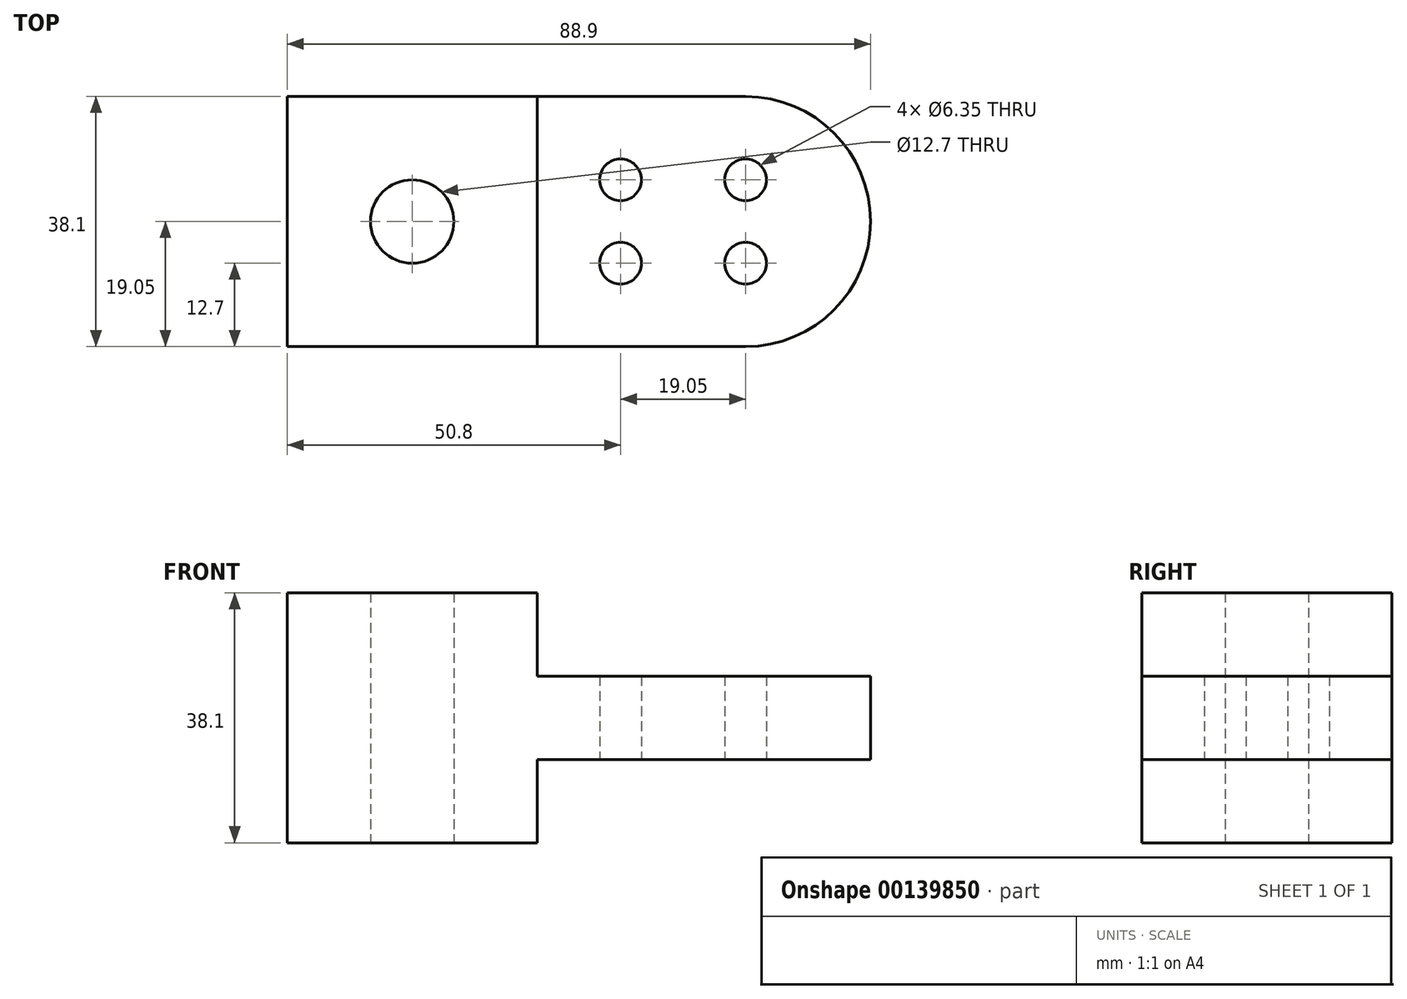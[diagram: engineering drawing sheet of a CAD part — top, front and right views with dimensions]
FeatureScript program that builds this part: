
annotation { "Feature Type Name" : "Feature", "Feature Type Description" : "" }
export const myFeature = defineFeature(function(context is Context, id is Id, definition is map)
    precondition{}
    {
        {
            var Q0;
            Q0=qCreatedBy(makeId("Top.planeOp"),FACE);
            var sketch = newSketch(context, id + "F0", { "sketchPlane" : qUnion([Q0])});
            skLineSegment(sketch, "E0.bottom", {"start": v(-69.85, 0) * mm, "end": v(0, 0) * mm});
            skLineSegment(sketch, "E0.top", {"start": v(-69.85, -38.1) * mm, "end": v(0, -38.1) * mm});
            skLineSegment(sketch, "E0.left", {"start": v(-69.85, 0) * mm, "end": v(-69.85, -38.1) * mm});
            skLineSegment(sketch, "E0.right", {"start": v(0, 0) * mm, "end": v(0, -38.1) * mm});
            skArc(sketch, "E1", {"start": v(0, -38.1) * mm, "mid": v(19.05, -19.05) * mm, "end": v(0, 0) * mm});
            skCircle(sketch, "E2", {"center": v(0, -12.7) * mm, "radius": 3.18 * mm});
            skCircle(sketch, "E3", {"center": v(0, -25.4) * mm, "radius": 3.18 * mm});
            skCircle(sketch, "E4", {"center": v(-19.05, -12.7) * mm, "radius": 3.18 * mm});
            skCircle(sketch, "E5", {"center": v(-19.05, -25.4) * mm, "radius": 3.18 * mm});
            skCircle(sketch, "E6", {"center": v(-50.8, -19.05) * mm, "radius": 6.35 * mm});
            skSolve(sketch);
        }
        {
            var Q0;
            Q0 = qSketchRegion(id + "F0", true);
            extrude(context, id + "F1", {"entities" : qUnion([Q0]), "depth" : 38.1 * mm});
        }
        {
            var Q0;
            Q0=qCreatedBy(makeId("Front.planeOp"),FACE);
            var sketch = newSketch(context, id + "F2", { "sketchPlane" : qUnion([Q0])});
            skLineSegment(sketch, "E7.bottom", {"start": v(0, 0) * mm, "end": v(-31.75, 0) * mm});
            skLineSegment(sketch, "E7.top", {"start": v(0, 12.7) * mm, "end": v(-31.75, 12.7) * mm});
            skLineSegment(sketch, "E7.left", {"start": v(0, 0) * mm, "end": v(0, 12.7) * mm});
            skLineSegment(sketch, "E7.right", {"start": v(-31.75, 0) * mm, "end": v(-31.75, 12.7) * mm});
            skLineSegment(sketch, "E8.bottom", {"start": v(0, 0) * mm, "end": v(19.05, 0) * mm});
            skLineSegment(sketch, "E8.top", {"start": v(0, 12.7) * mm, "end": v(19.05, 12.7) * mm});
            skLineSegment(sketch, "E8.right", {"start": v(19.05, 0) * mm, "end": v(19.05, 12.7) * mm});
            skLineSegment(sketch, "E9.bottom", {"start": v(0, 0) * mm, "end": v(-6.38, 0) * mm});
            skLineSegment(sketch, "E9.top", {"start": v(0, 25.4) * mm, "end": v(-6.38, 25.4) * mm});
            skLineSegment(sketch, "E9.left", {"start": v(0, 0) * mm, "end": v(0, 25.4) * mm});
            skLineSegment(sketch, "E9.right", {"start": v(-6.38, 0) * mm, "end": v(-6.38, 25.4) * mm});
            skLineSegment(sketch, "E10.bottom", {"start": v(0, 25.4) * mm, "end": v(-31.75, 25.4) * mm});
            skLineSegment(sketch, "E10.top", {"start": v(0, 38.1) * mm, "end": v(-31.75, 38.1) * mm});
            skPoint(sketch, "E11.oppositeSnap0", {"position": v(0, 38.1) * mm});
            skLineSegment(sketch, "E11.bottom", {"start": v(0, 25.4) * mm, "end": v(19.05, 25.4) * mm});
            skLineSegment(sketch, "E11.top", {"start": v(0, 38.1) * mm, "end": v(19.05, 38.1) * mm});
            skLineSegment(sketch, "E11.right", {"start": v(19.05, 25.4) * mm, "end": v(19.05, 38.1) * mm});
            skLineSegment(sketch, "E12", {"start": v(-31.75, 38.1) * mm, "end": v(-31.75, 25.4) * mm});
            skSolve(sketch);
        }
        {
            var Q0;
            {var subQ0=sQuery(id+"F2.wireOp",EDGE,"E7.bottom");Q0=makeQuery(id+"F2.imprint","IMPRINT",FACE,{"disambiguationData":[TD([[makeQuery(id+"F2.imprint","IMPRINT",EDGE,{"derivedFrom":subQ0}),-1.0]])]});}
            var Q1;
            {var subQ0=sQuery(id+"F2.wireOp",EDGE,"E8.bottom");Q1=makeQuery(id+"F2.imprint","IMPRINT",FACE,{"disambiguationData":[TD([[makeQuery(id+"F2.imprint","IMPRINT",EDGE,{"derivedFrom":subQ0}),1.0]])]});}
            var Q2;
            Q2=makeQuery(id+"F2.imprint","IMPRINT",FACE,{"disambiguationData":[TD([[makeQuery(id+"F2.imprint","IMPRINT",EDGE,{"derivedFrom":sQuery(id+"F2.wireOp",EDGE,"E10.top")}),1.0]])]});
            var Q3;
            {var subQ5=sQuery(id+"F2.wireOp",EDGE,"E9.bottom");Q3=makeQuery(id+"F2.imprint","IMPRINT",FACE,{"disambiguationData":[TD([[makeQuery(id+"F2.imprint","IMPRINT",EDGE,{"derivedFrom":subQ5}),-1.0]])]});}
            extrude(context, id + "F3", {"entities" : qUnion([Q0, Q1, Q2, Q3]), "operationType" : NewBodyOperationType.REMOVE, "endBound" : BoundingType.THROUGH_ALL, "depth" : 25.4 * mm});
        }
    });
